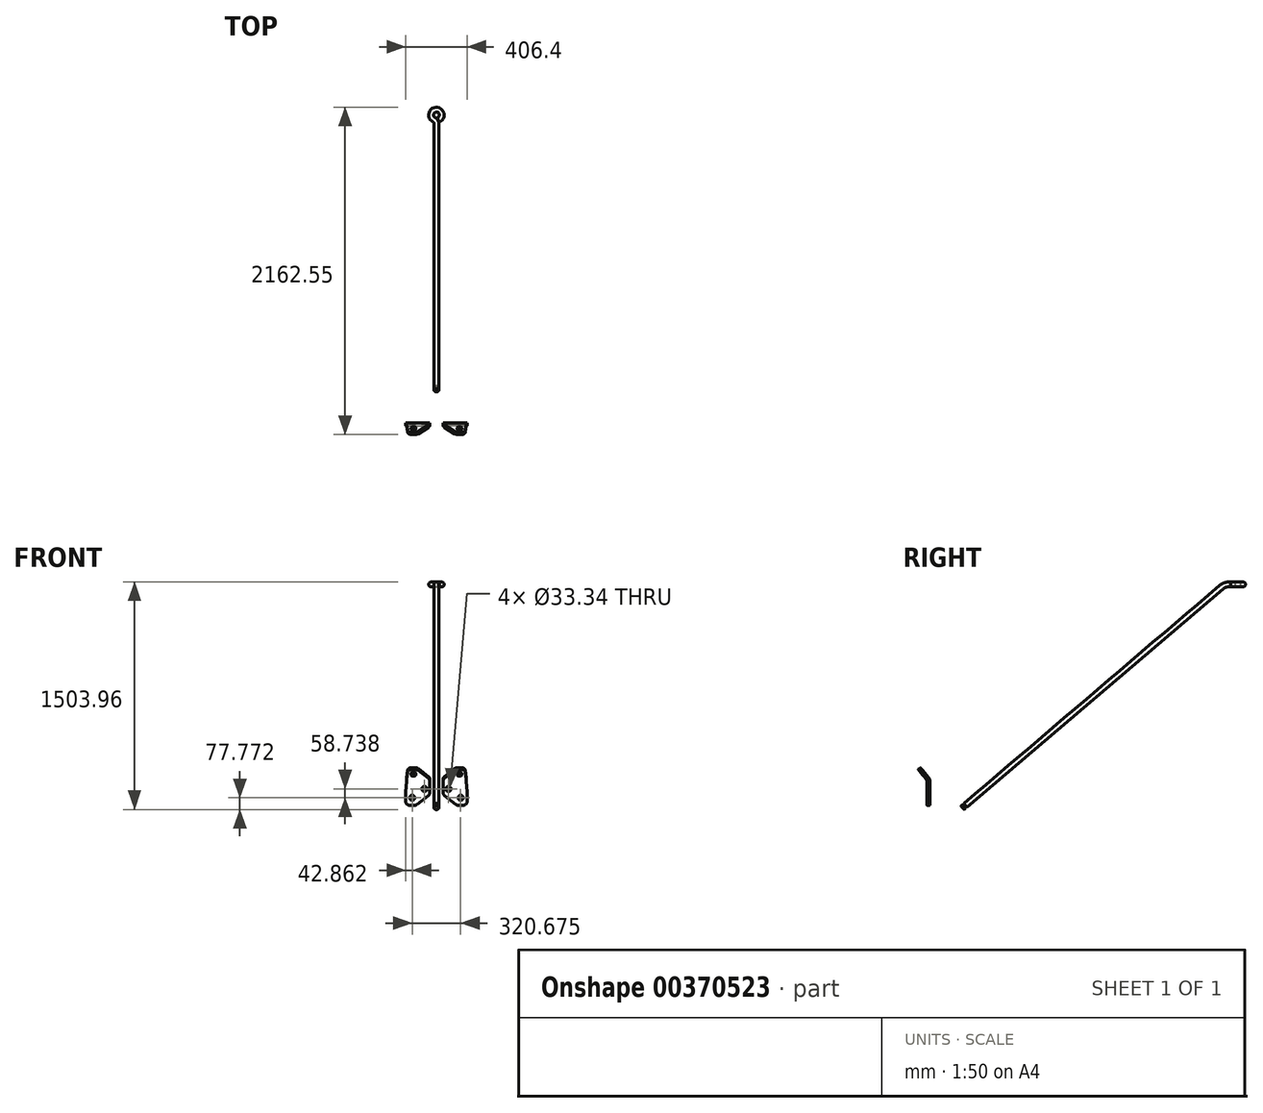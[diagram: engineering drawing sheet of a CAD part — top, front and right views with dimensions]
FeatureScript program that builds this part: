
annotation { "Feature Type Name" : "Feature", "Feature Type Description" : "" }
export const myFeature = defineFeature(function(context is Context, id is Id, definition is map)
    precondition{}
    {
        {
            var Q0;
            Q0=qCreatedBy(makeId("Front.planeOp"),FACE);
            var sketch = newSketch(context, id + "F0", { "sketchPlane" : qUnion([Q0])});
            skLineSegment(sketch, "E0", {"start": v(-177.8, 0) * mm, "end": v(-142.88, 0) * mm});
            skLineSegment(sketch, "E1", {"start": v(-127.22, 5.4) * mm, "end": v(-54.2, 62.55) * mm});
            skLineSegment(sketch, "E2", {"start": v(-44.45, 82.55) * mm, "end": v(-44.45, 165.1) * mm});
            skLineSegment(sketch, "E3", {"start": v(-44.45, 165.1) * mm, "end": v(-120.94, 248.9) * mm});
            skLineSegment(sketch, "E4", {"start": v(-139.7, 257.18) * mm, "end": v(-165.1, 257.18) * mm});
            skLineSegment(sketch, "E5", {"start": v(-203.2, 25.4) * mm, "end": v(-203.2, 85.73) * mm});
            skLineSegment(sketch, "E6", {"start": v(-203.1, 87.93) * mm, "end": v(-190.4, 233.98) * mm});
            skPoint(sketch, "E7.visualSharp", {"position": v(-203.2, 0) * mm});
            skArc(sketch, "E7.filletArc", {"start": v(-203.2, 25.4) * mm, "mid": v(-195.76, 7.44) * mm, "end": v(-177.8, 0) * mm});
            skPoint(sketch, "E8.visualSharp", {"position": v(-134.12, 0) * mm});
            skArc(sketch, "E8.filletArc", {"start": v(-142.88, 0) * mm, "mid": v(-134.6, 1.39) * mm, "end": v(-127.22, 5.4) * mm});
            skPoint(sketch, "E9.visualSharp", {"position": v(-44.45, 70.17) * mm});
            skArc(sketch, "E9.filletArc", {"start": v(-54.2, 62.55) * mm, "mid": v(-47.02, 71.42) * mm, "end": v(-44.45, 82.55) * mm});
            skPoint(sketch, "E10.visualSharp", {"position": v(-128.5, 257.18) * mm});
            skArc(sketch, "E10.filletArc", {"start": v(-120.94, 248.9) * mm, "mid": v(-129.45, 255.01) * mm, "end": v(-139.7, 257.18) * mm});
            skPoint(sketch, "E11.visualSharp", {"position": v(-188.39, 257.18) * mm});
            skArc(sketch, "E11.filletArc", {"start": v(-165.1, 257.18) * mm, "mid": v(-182.26, 250.5) * mm, "end": v(-190.4, 233.98) * mm});
            skPoint(sketch, "E12.visualSharp", {"position": v(-203.2, 86.83) * mm});
            skArc(sketch, "E12.filletArc", {"start": v(-203.1, 87.93) * mm, "mid": v(-203.18, 86.83) * mm, "end": v(-203.2, 85.73) * mm});
            skCircle(sketch, "E13", {"center": v(-152.4, 215.9) * mm, "radius": 16.67 * mm});
            skCircle(sketch, "E14", {"center": v(-160.34, 49.21) * mm, "radius": 16.67 * mm});
            skCircle(sketch, "E15", {"center": v(-79.38, 107.95) * mm, "radius": 16.67 * mm});
            skLineSegment(sketch, "E16", {"start": v(-196.4, 165.1) * mm, "end": v(-44.45, 165.1) * mm});
            skPoint(sketch, "E17.orphan", {"position": v(-209.96, 165.1) * mm});
            skLineSegment(sketch, "E18", {"start": v(-196.95, 158.75) * mm, "end": v(-44.45, 158.75) * mm});
            skSolve(sketch);
        }
        {
            var Q0;
            Q0=sQuery(id+"F0.wireOp",EDGE,"E16");
            var Q1;
            Q1=makeQuery(id+"F0.imprint","IMPRINT",FACE,{"disambiguationData":[TD([[makeQuery(id+"F0.imprint","IMPRINT",EDGE,{"derivedFrom":sQuery(id+"F0.wireOp",EDGE,"E0")}),1.0]])]});
            cPlane(context, id + "F1", {"entities" : qUnion([Q0, Q1]), "cplaneType" : CPlaneType.LINE_ANGLE, "offset" : 25.4 * mm, "angle" : 39 * degree, "width" : 152.4 * mm, "height" : 152.4 * mm});
        }
        {
            var Q0;
            Q0=qCreatedBy(id+"F1.planeOp",FACE);
            var sketch = newSketch(context, id + "F2", { "sketchPlane" : qUnion([Q0])});
            skLineSegment(sketch, "E19.0", {"start": v(196.4, 128.3) * mm, "end": v(44.45, 128.3) * mm});
            skLineSegment(sketch, "E20.0", {"start": v(203.2, 19.74) * mm, "end": v(203.2, 66.62) * mm});
            skCircle(sketch, "E21", {"center": v(152.4, 179.1) * mm, "radius": 16.67 * mm});
            skLineSegment(sketch, "E22", {"start": v(165.1, 220.38) * mm, "end": v(139.7, 220.38) * mm});
            skPoint(sketch, "E23.visualSharp", {"position": v(188.39, 220.38) * mm});
            skArc(sketch, "E23.filletArc", {"start": v(190.38, 197.4) * mm, "mid": v(182.18, 213.78) * mm, "end": v(165.1, 220.38) * mm});
            skPoint(sketch, "E24.visualSharp", {"position": v(128.5, 220.38) * mm});
            skArc(sketch, "E24.filletArc", {"start": v(139.7, 220.38) * mm, "mid": v(129.9, 218.42) * mm, "end": v(121.62, 212.83) * mm});
            skLineSegment(sketch, "E25", {"start": v(196.4, 128.3) * mm, "end": v(196.4, 134.66) * mm});
            skLineSegment(sketch, "E26", {"start": v(196.4, 134.66) * mm, "end": v(44.45, 134.66) * mm});
            skLineSegment(sketch, "E27", {"start": v(44.45, 134.66) * mm, "end": v(121.62, 212.83) * mm});
            skLineSegment(sketch, "E28", {"start": v(196.4, 134.66) * mm, "end": v(190.38, 197.4) * mm});
            skSolve(sketch);
        }
        {
            var Q0;
            Q0=makeQuery(id+"F0.imprint","IMPRINT",FACE,{"disambiguationData":[TD([[makeQuery(id+"F0.imprint","IMPRINT",EDGE,{"derivedFrom":sQuery(id+"F0.wireOp",EDGE,"E0")}),1.0]])]});
            extrude(context, id + "F3", {"entities" : qUnion([Q0]), "oppositeDirection" : true, "depth" : 19.05 * mm, "offsetDistance" : 25.4 * mm});
        }
        {
            var Q0;
            Q0=makeQuery(id+"F2.imprint","IMPRINT",FACE,{"disambiguationData":[TD([[makeQuery(id+"F2.imprint","IMPRINT",EDGE,{"derivedFrom":sQuery(id+"F2.wireOp",EDGE,"E21")}),-1.0]])]});
            extrude(context, id + "F4", {"entities" : qUnion([Q0]), "depth" : 19.05 * mm, "offsetDistance" : 25.4 * mm});
        }
        {
            var Q0;
            Q0=makeQuery(id+"F4.opExtrude","SWEPT_FACE",FACE,{"disambiguationData":[OSD([sQuery(id+"F2.wireOp",EDGE,"E26")])]});
            var Q1;
            Q1=makeQuery(id+"F3.opExtrude","SWEPT_FACE",FACE,{"disambiguationData":[OSD([sQuery(id+"F0.wireOp",EDGE,"E18")])]});
            loft(context, id + "F5", {"operationType" : NewBodyOperationType.ADD, "sheetProfilesArray" : [{ "sheetProfileEntities" : qUnion([Q0]) }, { "sheetProfileEntities" : qUnion([Q1]) }], "startCondition" : LoftEndDerivativeType.NORMAL_TO_PROFILE, "startMagnitude" : 1, "endCondition" : LoftEndDerivativeType.NORMAL_TO_PROFILE, "endMagnitude" : 1});
        }
        {
            var Q0;
            {var subQ0=sQuery(id+"F2.wireOp",EDGE,"E27");var subQ1=sQuery(id+"F2.wireOp",EDGE,"E26");Q0=makeQuery(id+"F5.boolean.opBoolean","MERGE",EDGE,{"derivedFrom":[makeQuery(id+"F4.opExtrude","SWEPT_EDGE",EDGE,{"disambiguationData":[OSD([subQ1,subQ0])]}),makeQuery(id+"F5.opLoft","MID_CAP_EDGE",EDGE,{"disambiguationData":[OSD([subQ1,subQ0])],"capPos":0.0})]});}
            fillet(context, id + "F6", {"entities" : qUnion([Q0]), "tangentPropagation" : true, "radius" : 25.4 * mm, "defaultsChanged" : false, "vertexSettings" : [], "allowEdgeOverflow" : false});
        }
        {
            var Q0;
            Q0=makeQuery(id+"F3.opExtrude","SWEPT_BODY",BODY,{"disambiguationData":[OSD([sQuery(id+"F0.wireOp",EDGE,"E0"),sQuery(id+"F0.wireOp",EDGE,"E1"),sQuery(id+"F0.wireOp",EDGE,"E2"),sQuery(id+"F0.wireOp",EDGE,"E5"),sQuery(id+"F0.wireOp",EDGE,"E6"),sQuery(id+"F0.wireOp",EDGE,"E7.filletArc"),sQuery(id+"F0.wireOp",EDGE,"E8.filletArc"),sQuery(id+"F0.wireOp",EDGE,"E9.filletArc"),sQuery(id+"F0.wireOp",EDGE,"E12.filletArc"),sQuery(id+"F0.wireOp",EDGE,"E14"),sQuery(id+"F0.wireOp",EDGE,"E15"),sQuery(id+"F0.wireOp",EDGE,"E18")])]});
            var Q1;
            Q1=qCreatedBy(makeId("Right.planeOp"),FACE);
            mirror(context, id + "F7", {"entities" : qUnion([Q0]), "mirrorPlane" : qUnion([Q1])});
        }
        {
            var Q0;
            Q0=qCreatedBy(makeId("Right.planeOp"),FACE);
            var sketch = newSketch(context, id + "F8", { "sketchPlane" : qUnion([Q0])});
            skLineSegment(sketch, "E29", {"start": v(254, 0) * mm, "end": v(1945.76, 1441.33) * mm});
            skLineSegment(sketch, "E30", {"start": v(0, 0) * mm, "end": v(678.45, 0) * mm, "construction": true});
            skPoint(sketch, "E31.visualSharp", {"position": v(1994.1, 1482.51) * mm});
            skArc(sketch, "E31.filletArc", {"start": v(1995.18, 1459.53) * mm, "mid": v(1968.85, 1454.84) * mm, "end": v(1945.76, 1441.33) * mm});
            skLineSegment(sketch, "E32", {"start": v(1995.18, 1383.33) * mm, "end": v(1995.18, 1459.53) * mm, "construction": true});
            skSolve(sketch);
        }
        {
            var Q0;
            Q0=qCreatedBy(makeId("Top.planeOp"),FACE);
            var Q1;
            Q1=sQuery(id+"F8.wireOp",VERTEX,"E31.filletArc.start");
            cPlane(context, id + "F9", {"entities" : qUnion([Q0, Q1]), "cplaneType" : CPlaneType.PLANE_POINT, "offset" : 25.4 * mm, "width" : 152.4 * mm, "height" : 152.4 * mm});
        }
        {
            var Q0;
            Q0=qCreatedBy(id+"F9.planeOp",FACE);
            var sketch = newSketch(context, id + "F10", { "sketchPlane" : qUnion([Q0])});
            skArc(sketch, "E33", {"start": v(-16.63, 2023.1) * mm, "mid": v(2.54, 2088.64) * mm, "end": v(12, 2021.01) * mm});
            skArc(sketch, "E34", {"start": v(-16.63, 2023.1) * mm, "mid": v(-4.47, 2011.43) * mm, "end": v(0, 1995.18) * mm});
            skPoint(sketch, "E35.0", {"position": v(0, 1995.18) * mm});
            skLineSegment(sketch, "E36.0", {"start": v(0, 1995.18) * mm, "end": v(0, 1945.76) * mm});
            skSolve(sketch);
        }
        {
            var Q0;
            Q0=sQuery(id+"F8.wireOp",VERTEX,"E29.start");
            var Q1;
            Q1=sQuery(id+"F8.wireOp",EDGE,"E29");
            cPlane(context, id + "F11", {"entities" : qUnion([Q0, Q1]), "cplaneType" : CPlaneType.LINE_POINT, "offset" : 25.4 * mm, "width" : 152.4 * mm, "height" : 152.4 * mm});
        }
        {
            var Q0;
            Q0=qCreatedBy(id+"F11.planeOp",FACE);
            var sketch = newSketch(context, id + "F12", { "sketchPlane" : qUnion([Q0])});
            skPoint(sketch, "E37.0", {"position": v(0, -164.72) * mm});
            skCircle(sketch, "E38", {"center": v(0, -164.72) * mm, "radius": 15.88 * mm});
            skSolve(sketch);
        }
        {
            var Q0;
            Q0=makeQuery(id+"F12.imprint","IMPRINT",FACE,{"disambiguationData":[TD([[makeQuery(id+"F12.imprint","IMPRINT",EDGE,{"derivedFrom":sQuery(id+"F12.wireOp",EDGE,"E38")}),1.0]])]});
            var Q1;
            Q1=sQuery(id+"F8.wireOp",EDGE,"E29");
            var Q2;
            Q2=sQuery(id+"F8.wireOp",EDGE,"E31.filletArc");
            var Q3;
            Q3=sQuery(id+"F10.wireOp",EDGE,"E34");
            var Q4;
            Q4=sQuery(id+"F10.wireOp",EDGE,"E33");
            sweep(context, id + "F13", {"profiles" : qUnion([Q0]), "path" : qUnion([Q1, Q2, Q3, Q4])});
        }
        {
            var Q0;
            Q0 = qSketchRegion(id + "F12", true);
            extrude(context, id + "F14", {"entities" : qUnion([Q0]), "oppositeDirection" : true, "depth" : 25.4 * mm, "offsetDistance" : 25.4 * mm, "hasSecondDirection" : true, "secondDirectionOppositeDirection" : true, "secondDirectionDepth" : 12.7 * mm});
        }
    });
